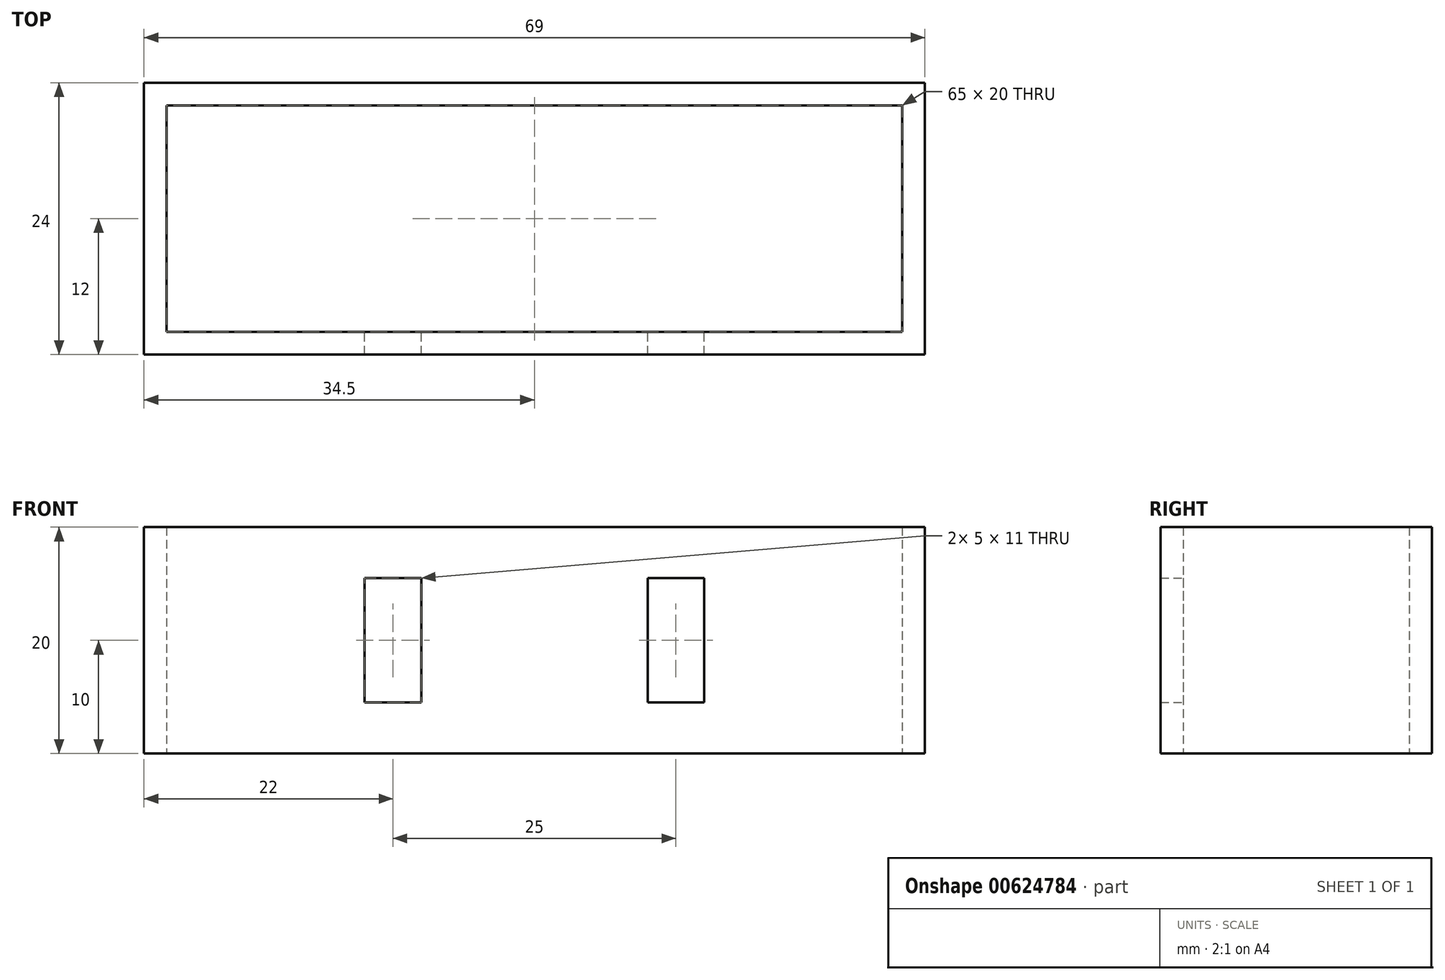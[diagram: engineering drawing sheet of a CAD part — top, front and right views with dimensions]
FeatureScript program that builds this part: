
annotation { "Feature Type Name" : "Feature", "Feature Type Description" : "" }
export const myFeature = defineFeature(function(context is Context, id is Id, definition is map)
    precondition{}
    {
        {
            var Q0;
            Q0=qCreatedBy(makeId("Front.planeOp"),FACE);
            var sketch = newSketch(context, id + "F0", { "sketchPlane" : qUnion([Q0])});
            skLineSegment(sketch, "E0.bottom", {"start": v(0, 0) * mm, "end": v(69, 0) * mm});
            skLineSegment(sketch, "E0.top", {"start": v(0, -20) * mm, "end": v(69, -20) * mm});
            skLineSegment(sketch, "E0.left", {"start": v(0, 0) * mm, "end": v(0, -20) * mm});
            skLineSegment(sketch, "E0.right", {"start": v(69, 0) * mm, "end": v(69, -20) * mm});
            skSolve(sketch);
        }
        {
            var Q0;
            Q0=qSketchRegion(id+"F0",true);
            extrude(context, id + "F1", {"entities" : qUnion([Q0]), "depth" : 24 * mm, "offsetDistance" : 25 * mm});
        }
        {
            var Q0;
            Q0=qCreatedBy(makeId("Top.planeOp"),FACE);
            var sketch = newSketch(context, id + "F2", { "sketchPlane" : qUnion([Q0])});
            skLineSegment(sketch, "E1.bottom", {"start": v(2, -2) * mm, "end": v(67, -2) * mm});
            skLineSegment(sketch, "E1.top", {"start": v(2, -22) * mm, "end": v(67, -22) * mm});
            skLineSegment(sketch, "E1.left", {"start": v(2, -2) * mm, "end": v(2, -22) * mm});
            skLineSegment(sketch, "E1.right", {"start": v(67, -2) * mm, "end": v(67, -22) * mm});
            skSolve(sketch);
        }
        {
            var Q0;
            Q0=qSketchRegion(id+"F2",true);
            extrude(context, id + "F3", {"entities" : qUnion([Q0]), "operationType" : NewBodyOperationType.REMOVE, "endBound" : BoundingType.SYMMETRIC, "depth" : 40 * mm, "offsetDistance" : 25 * mm});
        }
        {
            var Q0;
            Q0=makeQuery(id+"F3.boolean.opBoolean","COPY",FACE,{"derivedFrom":makeQuery(id+"F3.opExtrude","SWEPT_FACE",FACE,{"disambiguationData":[OSD([sQuery(id+"F2.wireOp",EDGE,"E1.top")])]})});
            cPlane(context, id + "F4", {"entities" : qUnion([Q0]), "cplaneType" : CPlaneType.OFFSET, "offset" : 0 * mm, "width" : 150 * mm, "height" : 150 * mm});
        }
        {
            var Q0;
            Q0=qCreatedBy(id+"F4.planeOp",FACE);
            var sketch = newSketch(context, id + "F5", { "sketchPlane" : qUnion([Q0])});
            skLineSegment(sketch, "E2.bottom", {"start": v(-24.5, -4.5) * mm, "end": v(-19.5, -4.5) * mm});
            skLineSegment(sketch, "E3.top", {"start": v(-24.5, -15.5) * mm, "end": v(-19.5, -15.5) * mm});
            skLineSegment(sketch, "E4", {"start": v(-24.5, -4.5) * mm, "end": v(-24.5, -15.5) * mm});
            skLineSegment(sketch, "E5", {"start": v(-19.5, -4.5) * mm, "end": v(-19.5, -15.5) * mm});
            skLineSegment(sketch, "E6", {"start": v(-34.5, 0) * mm, "end": v(-34.5, -20) * mm, "construction": true});
            skLineSegment(sketch, "E7", {"start": v(0, -10) * mm, "end": v(-69, -10) * mm, "construction": true});
            skPoint(sketch, "E8", {"position": v(-34.5, -10) * mm});
            skPoint(sketch, "E9", {"position": v(-20.5, 2.87) * mm});
            skLineSegment(sketch, "E10.bottom", {"start": v(-49.5, -4.5) * mm, "end": v(-44.5, -4.5) * mm});
            skLineSegment(sketch, "E11.top", {"start": v(-49.5, -15.5) * mm, "end": v(-44.5, -15.5) * mm});
            skLineSegment(sketch, "E12", {"start": v(-49.5, -4.5) * mm, "end": v(-49.5, -15.5) * mm});
            skLineSegment(sketch, "E13", {"start": v(-44.5, -4.5) * mm, "end": v(-44.5, -15.5) * mm});
            skSolve(sketch);
        }
        {
            var Q0;
            Q0=qSketchRegion(id+"F5",true);
            extrude(context, id + "F6", {"entities" : qUnion([Q0]), "operationType" : NewBodyOperationType.REMOVE, "oppositeDirection" : true, "depth" : 5 * mm, "offsetDistance" : 25 * mm});
        }
    });
